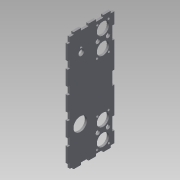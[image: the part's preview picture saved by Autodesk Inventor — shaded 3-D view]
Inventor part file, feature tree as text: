
AUTODESK INVENTOR PART (.ipt)
format: ipt  version: 2015 SP1 (Build 190203100, 203)  size: 200,192 bytes
history: native  units: mm
features: extrude x1, sketch x1
ambient origin geometry x8: Origin, YZ Plane, XZ Plane, XY Plane, X Axis, Y Axis, Z Axis, Center Point
bodies: Solid1 (feature_tree)
feature tree (2):
  extrude  "Extrusion1"  Depth=3.0mm
  sketch  "Sketch1"  dims[d0=7.8mm d1=7.8mm d2=7.8mm d3=7.8mm d7=3.0mm d8=20.0mm d9=30.0mm d11=30.0mm d12=30.0mm d14=30.0mm d17=10.0mm d18=3.0mm d19=20.0mm d21=20.0mm d22=20.0mm d24=20.0mm d27=3.0mm d28=0.0mm]
